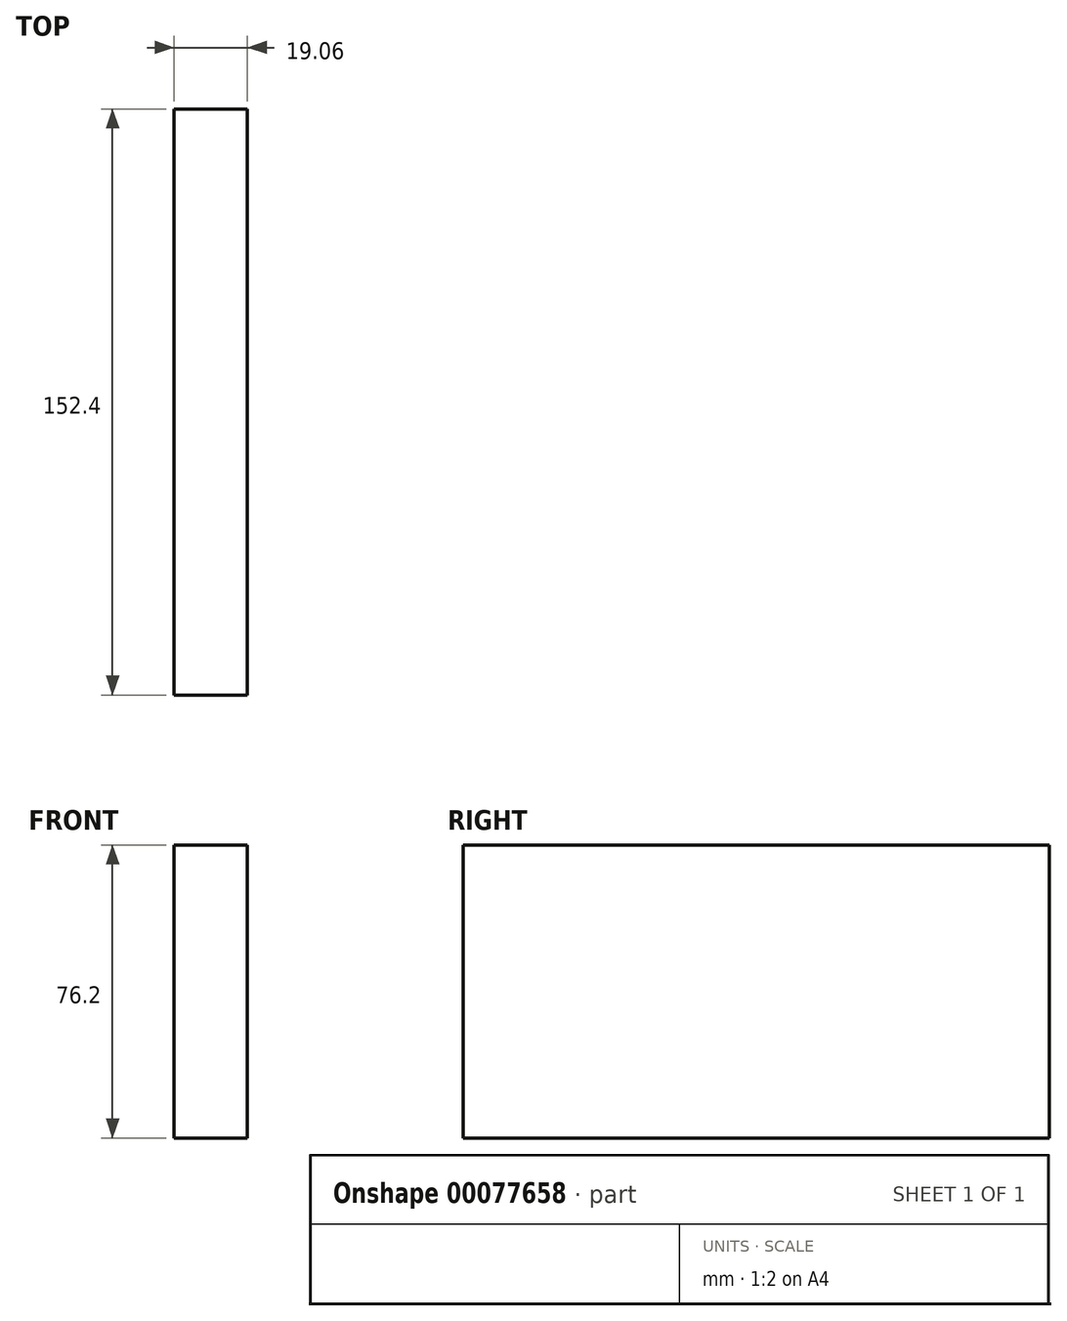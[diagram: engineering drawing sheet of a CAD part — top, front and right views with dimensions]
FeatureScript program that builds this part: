
annotation { "Feature Type Name" : "Feature", "Feature Type Description" : "" }
export const myFeature = defineFeature(function(context is Context, id is Id, definition is map)
    precondition{}
    {
        {
            var Q0;
            Q0=qCreatedBy(makeId("Front.planeOp"),FACE);
            var sketch = newSketch(context, id + "F0", { "sketchPlane" : qUnion([Q0])});
            skLineSegment(sketch, "E0", {"start": v(-9.53, 38.1) * mm, "end": v(9.53, 38.1) * mm});
            skLineSegment(sketch, "E1", {"start": v(9.53, 38.1) * mm, "end": v(9.53, -38.1) * mm});
            skLineSegment(sketch, "E2", {"start": v(9.53, -38.1) * mm, "end": v(-9.53, -38.1) * mm});
            skLineSegment(sketch, "E3", {"start": v(-9.53, -38.1) * mm, "end": v(-9.53, 38.1) * mm});
            skSolve(sketch);
        }
        {
            var Q0;
            Q0=makeQuery(id+"F0.imprint","IMPRINT",FACE,{"disambiguationData":[TD([[makeQuery(id+"F0.imprint","IMPRINT",EDGE,{"derivedFrom":sQuery(id+"F0.wireOp",EDGE,"E0")}),-1.0]])]});
            extrude(context, id + "F1", {"entities" : qUnion([Q0]), "depth" : 152.4 * mm});
        }
    });
